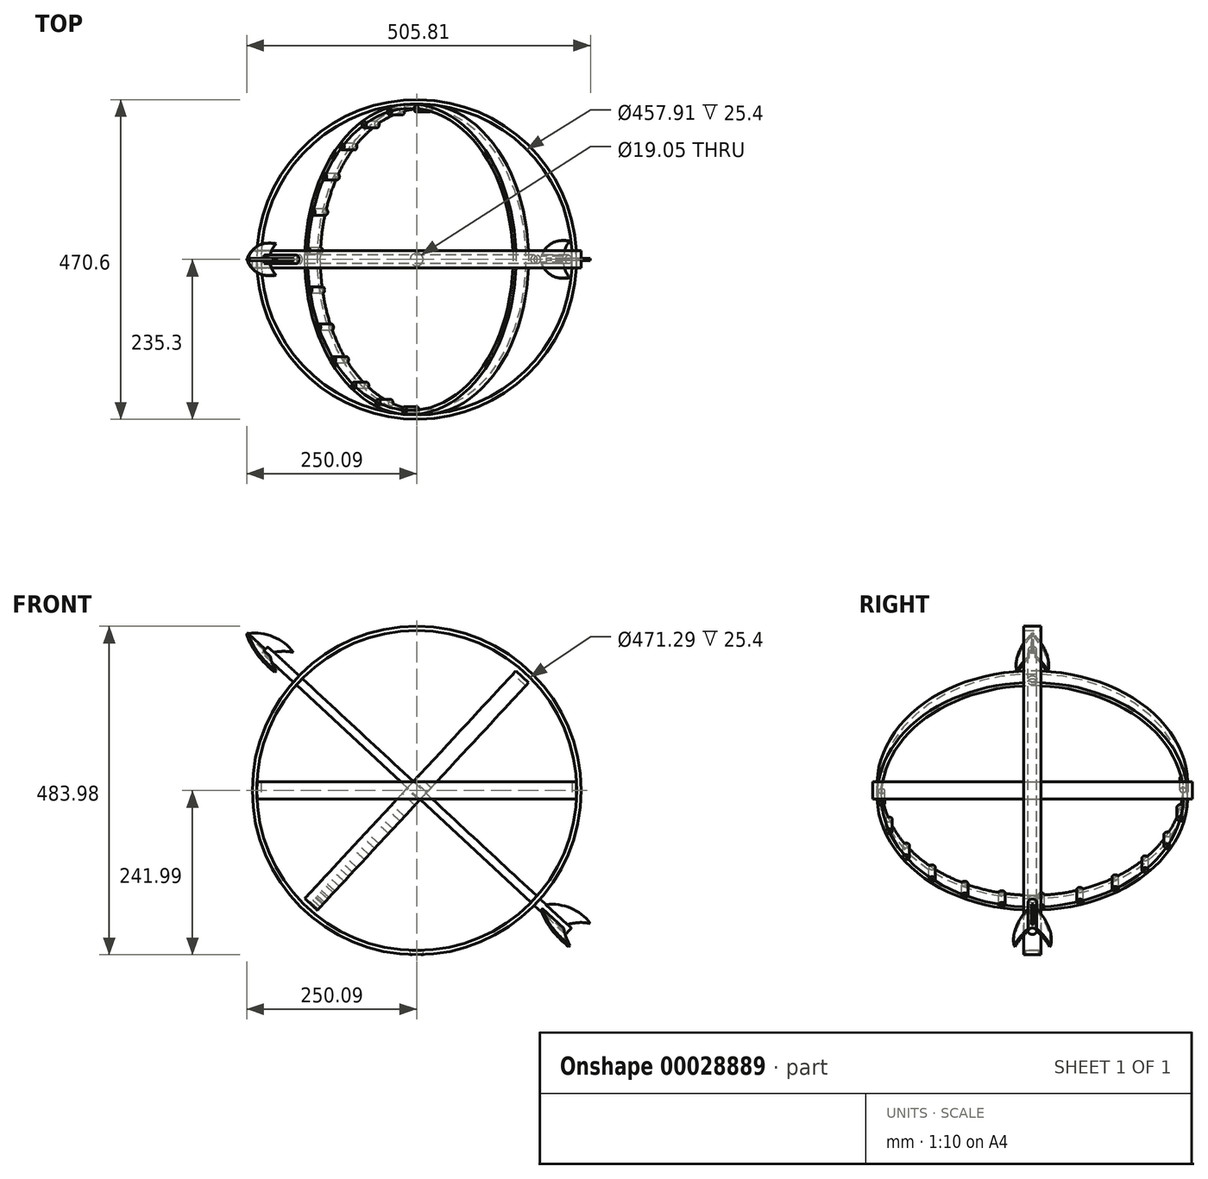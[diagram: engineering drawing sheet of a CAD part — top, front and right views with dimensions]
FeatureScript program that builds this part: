
annotation { "Feature Type Name" : "Feature", "Feature Type Description" : "" }
export const myFeature = defineFeature(function(context is Context, id is Id, definition is map)
    precondition{}
    {
        {
            var Q0;
            Q0=qCreatedBy(makeId("Top.planeOp"),FACE);
            var sketch = newSketch(context, id + "F0", { "sketchPlane" : qUnion([Q0])});
            skLineSegment(sketch, "E0", {"start": v(0, 0) * mm, "end": v(0, -151.73) * mm});
            skSolve(sketch);
        }
        {
            var Q0;
            Q0=sQuery(id+"F0.wireOp",EDGE,"E0");
            cPlane(context, id + "F1", {"entities" : qUnion([Q0]), "cplaneType" : CPlaneType.LINE_ANGLE, "offset" : 152.4 * mm, "angle" : 47.16 * degree, "width" : 152.4 * mm, "height" : 152.4 * mm});
        }
        {
            var Q0;
            Q0=qCreatedBy(id+"F1.planeOp",FACE);
            var sketch = newSketch(context, id + "F2", { "sketchPlane" : qUnion([Q0])});
            skCircle(sketch, "E1", {"center": v(0, 0) * mm, "radius": 222.25 * mm});
            skCircle(sketch, "E2.0", {"center": v(0, 0) * mm, "radius": 228.6 * mm});
            skCircle(sketch, "E3", {"center": v(0, 0) * mm, "radius": 6.35 * mm});
            skSolve(sketch);
        }
        {
            var Q0;
            Q0=makeQuery(id+"F2.imprint","IMPRINT",FACE,{"disambiguationData":[TD([[makeQuery(id+"F2.imprint","IMPRINT",EDGE,{"derivedFrom":sQuery(id+"F2.wireOp",EDGE,"E2.0")}),1.0]])]});
            extrude(context, id + "F3", {"entities" : qUnion([Q0]), "depth" : 12.7 * mm, "hasSecondDirection" : true, "secondDirectionOppositeDirection" : true, "secondDirectionDepth" : 12.7 * mm});
        }
        {
            var Q0;
            Q0=qCreatedBy(makeId("Top.planeOp"),FACE);
            var sketch = newSketch(context, id + "F4", { "sketchPlane" : qUnion([Q0])});
            skCircle(sketch, "E4", {"center": v(0, 0) * mm, "radius": 228.95 * mm});
            skCircle(sketch, "E5.0", {"center": v(0, 0) * mm, "radius": 235.3 * mm});
            skSolve(sketch);
        }
        {
            var Q0;
            Q0=makeQuery(id+"F4.imprint","IMPRINT",FACE,{"disambiguationData":[TD([[makeQuery(id+"F4.imprint","IMPRINT",EDGE,{"derivedFrom":sQuery(id+"F4.wireOp",EDGE,"E4")}),-1.0]])]});
            extrude(context, id + "F5", {"entities" : qUnion([Q0]), "depth" : 12.7 * mm, "hasSecondDirection" : true, "secondDirectionOppositeDirection" : true, "secondDirectionDepth" : 12.7 * mm});
        }
        {
            var Q0;
            Q0=qCreatedBy(makeId("Front.planeOp"),FACE);
            var sketch = newSketch(context, id + "F6", { "sketchPlane" : qUnion([Q0])});
            skCircle(sketch, "E6", {"center": v(0, 0) * mm, "radius": 235.64 * mm});
            skCircle(sketch, "E7.0", {"center": v(0, 0) * mm, "radius": 242 * mm});
            skSolve(sketch);
        }
        {
            var Q0;
            Q0=makeQuery(id+"F6.imprint","IMPRINT",FACE,{"disambiguationData":[TD([[makeQuery(id+"F6.imprint","IMPRINT",EDGE,{"derivedFrom":sQuery(id+"F6.wireOp",EDGE,"E6")}),-1.0]])]});
            extrude(context, id + "F7", {"entities" : qUnion([Q0]), "depth" : 12.7 * mm, "hasSecondDirection" : true, "secondDirectionOppositeDirection" : true, "secondDirectionDepth" : 12.7 * mm});
        }
        {
            var Q0;
            Q0=makeQuery(id+"F2.imprint","IMPRINT",FACE,{"disambiguationData":[TD([[makeQuery(id+"F2.imprint","IMPRINT",EDGE,{"derivedFrom":sQuery(id+"F2.wireOp",EDGE,"E3")}),1.0]])]});
            extrude(context, id + "F8", {"entities" : qUnion([Q0]), "operationType" : NewBodyOperationType.ADD, "depth" : 304.8 * mm, "hasSecondDirection" : true, "secondDirectionOppositeDirection" : true, "secondDirectionDepth" : 304.8 * mm});
        }
        {
            var Q0;
            Q0=qCreatedBy(makeId("Top.planeOp"),FACE);
            cPlane(context, id + "F9", {"entities" : qUnion([Q0]), "cplaneType" : CPlaneType.OFFSET, "offset" : 76.2 * mm, "oppositeDirection" : true, "width" : 152.4 * mm, "height" : 152.4 * mm});
        }
        {
            var Q0;
            Q0=qCreatedBy(id+"F9.planeOp",FACE);
            var sketch = newSketch(context, id + "F10", { "sketchPlane" : qUnion([Q0])});
            skCircle(sketch, "E8", {"center": v(0, 0) * mm, "radius": 9.53 * mm});
            skSolve(sketch);
        }
        {
            var Q0;
            Q0 = qSketchRegion(id + "F10", true);
            extrude(context, id + "F11", {"entities" : qUnion([Q0]), "operationType" : NewBodyOperationType.REMOVE, "oppositeDirection" : true, "depth" : 609.6 * mm});
        }
        {
            var Q0;
            Q0=qCreatedBy(id+"F1.planeOp",FACE);
            var sketch = newSketch(context, id + "F12", { "sketchPlane" : qUnion([Q0])});
            skCircle(sketch, "E9.0", {"center": v(0, 0) * mm, "radius": 222.25 * mm, "construction": true});
            skLineSegment(sketch, "E10", {"start": v(0, 0) * mm, "end": v(0, -222.25) * mm, "construction": true});
            skCircle(sketch, "E11", {"center": v(12.87, -221.88) * mm, "radius": 4.76 * mm});
            skCircle(sketch, "E12.1.0", {"center": v(69.85, -210.99) * mm, "radius": 4.76 * mm});
            skCircle(sketch, "E12.2.0", {"center": v(122.08, -185.72) * mm, "radius": 4.76 * mm});
            skCircle(sketch, "E12.3.0", {"center": v(165.99, -147.8) * mm, "radius": 4.76 * mm});
            skCircle(sketch, "E12.4.0", {"center": v(198.58, -99.8) * mm, "radius": 4.76 * mm});
            skCircle(sketch, "E12.5.0", {"center": v(217.65, -45) * mm, "radius": 4.76 * mm});
            skCircle(sketch, "E12.6.0", {"center": v(221.88, 12.87) * mm, "radius": 4.76 * mm});
            skCircle(sketch, "E12.7.0", {"center": v(210.99, 69.85) * mm, "radius": 4.76 * mm});
            skCircle(sketch, "E12.8.0", {"center": v(185.72, 122.08) * mm, "radius": 4.76 * mm});
            skCircle(sketch, "E12.9.0", {"center": v(147.8, 165.99) * mm, "radius": 4.76 * mm});
            skCircle(sketch, "E12.10.0", {"center": v(99.8, 198.58) * mm, "radius": 4.76 * mm});
            skCircle(sketch, "E12.11.0", {"center": v(45, 217.65) * mm, "radius": 4.76 * mm});
            skCircle(sketch, "E12.12.0", {"center": v(-12.87, 221.88) * mm, "radius": 4.76 * mm});
            skCircle(sketch, "E12.13.0", {"center": v(-69.85, 210.99) * mm, "radius": 4.76 * mm});
            skCircle(sketch, "E12.14.0", {"center": v(-122.08, 185.72) * mm, "radius": 4.76 * mm});
            skCircle(sketch, "E12.15.0", {"center": v(-165.99, 147.8) * mm, "radius": 4.76 * mm});
            skCircle(sketch, "E12.16.0", {"center": v(-198.58, 99.8) * mm, "radius": 4.76 * mm});
            skCircle(sketch, "E12.17.0", {"center": v(-217.65, 45) * mm, "radius": 4.76 * mm});
            skCircle(sketch, "E12.18.0", {"center": v(-221.88, -12.87) * mm, "radius": 4.76 * mm});
            skCircle(sketch, "E12.19.0", {"center": v(-210.99, -69.85) * mm, "radius": 4.76 * mm});
            skCircle(sketch, "E12.20.0", {"center": v(-185.72, -122.08) * mm, "radius": 4.76 * mm});
            skCircle(sketch, "E12.21.0", {"center": v(-147.8, -165.99) * mm, "radius": 4.76 * mm});
            skCircle(sketch, "E12.22.0", {"center": v(-99.8, -198.58) * mm, "radius": 4.76 * mm});
            skCircle(sketch, "E12.23.0", {"center": v(-45, -217.65) * mm, "radius": 4.76 * mm});
            skLineSegment(sketch, "E13", {"start": v(0, 0) * mm, "end": v(12.87, -221.88) * mm, "construction": true});
            skSolve(sketch);
        }
        {
            var Q0;
            Q0=makeQuery(id+"F12.imprint","IMPRINT",FACE,{"disambiguationData":[TD([[makeQuery(id+"F12.imprint","IMPRINT",EDGE,{"derivedFrom":sQuery(id+"F12.wireOp",EDGE,"E11")}),1.0]])]});
            var Q1;
            Q1=makeQuery(id+"F12.imprint","IMPRINT",FACE,{"disambiguationData":[TD([[makeQuery(id+"F12.imprint","IMPRINT",EDGE,{"derivedFrom":sQuery(id+"F12.wireOp",EDGE,"E12.1.0")}),1.0]])]});
            var Q2;
            Q2=makeQuery(id+"F12.imprint","IMPRINT",FACE,{"disambiguationData":[TD([[makeQuery(id+"F12.imprint","IMPRINT",EDGE,{"derivedFrom":sQuery(id+"F12.wireOp",EDGE,"E12.2.0")}),1.0]])]});
            var Q3;
            Q3=makeQuery(id+"F12.imprint","IMPRINT",FACE,{"disambiguationData":[TD([[makeQuery(id+"F12.imprint","IMPRINT",EDGE,{"derivedFrom":sQuery(id+"F12.wireOp",EDGE,"E12.3.0")}),1.0]])]});
            var Q4;
            Q4=makeQuery(id+"F12.imprint","IMPRINT",FACE,{"disambiguationData":[TD([[makeQuery(id+"F12.imprint","IMPRINT",EDGE,{"derivedFrom":sQuery(id+"F12.wireOp",EDGE,"E12.23.0")}),1.0]])]});
            var Q5;
            Q5=makeQuery(id+"F12.imprint","IMPRINT",FACE,{"disambiguationData":[TD([[makeQuery(id+"F12.imprint","IMPRINT",EDGE,{"derivedFrom":sQuery(id+"F12.wireOp",EDGE,"E12.4.0")}),1.0]])]});
            var Q6;
            Q6=makeQuery(id+"F12.imprint","IMPRINT",FACE,{"disambiguationData":[TD([[makeQuery(id+"F12.imprint","IMPRINT",EDGE,{"derivedFrom":sQuery(id+"F12.wireOp",EDGE,"E12.5.0")}),1.0]])]});
            var Q7;
            Q7=makeQuery(id+"F12.imprint","IMPRINT",FACE,{"disambiguationData":[TD([[makeQuery(id+"F12.imprint","IMPRINT",EDGE,{"derivedFrom":sQuery(id+"F12.wireOp",EDGE,"E12.22.0")}),1.0]])]});
            var Q8;
            Q8=makeQuery(id+"F12.imprint","IMPRINT",FACE,{"disambiguationData":[TD([[makeQuery(id+"F12.imprint","IMPRINT",EDGE,{"derivedFrom":sQuery(id+"F12.wireOp",EDGE,"E12.21.0")}),1.0]])]});
            var Q9;
            Q9=makeQuery(id+"F12.imprint","IMPRINT",FACE,{"disambiguationData":[TD([[makeQuery(id+"F12.imprint","IMPRINT",EDGE,{"derivedFrom":sQuery(id+"F12.wireOp",EDGE,"E12.20.0")}),1.0]])]});
            var Q10;
            Q10=makeQuery(id+"F12.imprint","IMPRINT",FACE,{"disambiguationData":[TD([[makeQuery(id+"F12.imprint","IMPRINT",EDGE,{"derivedFrom":sQuery(id+"F12.wireOp",EDGE,"E12.19.0")}),1.0]])]});
            var Q11;
            Q11=makeQuery(id+"F12.imprint","IMPRINT",FACE,{"disambiguationData":[TD([[makeQuery(id+"F12.imprint","IMPRINT",EDGE,{"derivedFrom":sQuery(id+"F12.wireOp",EDGE,"E12.6.0")}),1.0]])]});
            var Q12;
            Q12=makeQuery(id+"F12.imprint","IMPRINT",FACE,{"disambiguationData":[TD([[makeQuery(id+"F12.imprint","IMPRINT",EDGE,{"derivedFrom":sQuery(id+"F12.wireOp",EDGE,"E12.18.0")}),1.0]])]});
            extrude(context, id + "F13", {"entities" : qUnion([Q0, Q1, Q2, Q3, Q4, Q5, Q6, Q7, Q8, Q9, Q10, Q11, Q12]), "depth" : 12.7 * mm, "hasSecondDirection" : true, "secondDirectionOppositeDirection" : true, "secondDirectionDepth" : 12.7 * mm});
        }
        {
            var Q0;
            Q0=qCreatedBy(makeId("Front.planeOp"),FACE);
            var sketch = newSketch(context, id + "F14", { "sketchPlane" : qUnion([Q0])});
            skLineSegment(sketch, "E14", {"start": v(181.7, -159.83) * mm, "end": v(227.81, -202.6) * mm, "construction": true});
            skLineSegment(sketch, "E15", {"start": v(219.18, -211.9) * mm, "end": v(173.07, -169.14) * mm, "construction": true});
            skLineSegment(sketch, "E16.0", {"start": v(227.81, -202.6) * mm, "end": v(219.18, -211.9) * mm, "construction": true});
            skCircle(sketch, "E17", {"center": v(198.96, -238.59) * mm, "radius": 71.03 * mm});
            skCircle(sketch, "E18", {"center": v(241.88, -260.98) * mm, "radius": 66.56 * mm});
            skLineSegment(sketch, "E19", {"start": v(226.68, -203.82) * mm, "end": v(180.61, -161.1) * mm});
            skSolve(sketch);
        }
        {
            var Q0;
            {var subQ0=sQuery(id+"F14.wireOp",EDGE,"E19");var subQ3=sQuery(id+"F14.wireOp",EDGE,"E17");var subQ4=makeQuery(id+"F14.imprint","INTERSECT",VERTEX,{"derivedFrom":[subQ3,subQ0]});Q0=makeQuery(id+"F14.imprint","IMPRINT",FACE,{"disambiguationData":[TD([[makeQuery(id+"F14.imprint","IMPRINT",EDGE,{"disambiguationData":[TD([[subQ4,1.0]])],"derivedFrom":subQ3}),1.0]])]});}
            extrude(context, id + "F15", {"entities" : qUnion([Q0]), "depth" : 1.59 * mm, "hasSecondDirection" : true, "secondDirectionOppositeDirection" : true, "secondDirectionDepth" : 1.59 * mm});
        }
        {
            var Q0;
            Q0=makeQuery(id+"F15.opExtrude","SWEPT_BODY",BODY,{"disambiguationData":[OSD([sQuery(id+"F14.wireOp",EDGE,"E14"),sQuery(id+"F14.wireOp",EDGE,"E17"),sQuery(id+"F14.wireOp",EDGE,"E18")])]});
            var Q1;
            Q1=makeQuery(id+"F8.opExtrude","CAP_EDGE",EDGE,{"disambiguationData":[OSD([sQuery(id+"F2.wireOp",EDGE,"E3")])],"isStart":false});
            var Q2;
            Q2=makeQuery(id+"F7.opExtrude","SWEPT_BODY",BODY,{"disambiguationData":[OSD([sQuery(id+"F6.wireOp",EDGE,"E6"),sQuery(id+"F6.wireOp",EDGE,"E7.0")])]});
            circularPattern(context, id + "F16", {"operationType" : NewBodyOperationType.ADD, "entities" : qUnion([Q0]), "axis" : qUnion([Q1]), "angle" : 120 * degree, "instanceCount" : 3});
        }
        {
            var Q0;
            Q0=qCreatedBy(makeId("Front.planeOp"),FACE);
            var sketch = newSketch(context, id + "F17", { "sketchPlane" : qUnion([Q0])});
            skLineSegment(sketch, "E20", {"start": v(-255.58, 239.59) * mm, "end": v(-209.47, 196.83) * mm, "construction": true});
            skLineSegment(sketch, "E21", {"start": v(-218.1, 187.52) * mm, "end": v(-264.21, 230.28) * mm, "construction": true});
            skLineSegment(sketch, "E22.0", {"start": v(-209.62, 196.66) * mm, "end": v(-218.25, 187.35) * mm, "construction": true});
            skCircle(sketch, "E23", {"center": v(-238.32, 160.84) * mm, "radius": 71.03 * mm});
            skCircle(sketch, "E24", {"center": v(-195.4, 138.44) * mm, "radius": 66.56 * mm});
            skLineSegment(sketch, "E25", {"start": v(-210.76, 195.44) * mm, "end": v(-302.12, 280.16) * mm});
            skLineSegment(sketch, "E26.0", {"start": v(-219.18, 211.9) * mm, "end": v(-227.81, 202.6) * mm});
            skPoint(sketch, "E27", {"position": v(-223.5, 207.25) * mm});
            skSolve(sketch);
        }
        {
            var Q0;
            {var subQ0=sQuery(id+"F17.wireOp",EDGE,"E25");var subQ1=makeQuery(id+"F17.imprint","IMPRINT",VERTEX,{"derivedFrom":subQ0});Q0=makeQuery(id+"F17.imprint","IMPRINT",FACE,{"disambiguationData":[TD([[makeQuery(id+"F17.imprint","IMPRINT",EDGE,{"disambiguationData":[TD([[subQ1,1.0]])],"derivedFrom":subQ0}),-1.0]])]});}
            extrude(context, id + "F18", {"entities" : qUnion([Q0]), "depth" : 1.59 * mm, "hasSecondDirection" : true, "secondDirectionOppositeDirection" : true, "secondDirectionDepth" : 1.59 * mm});
        }
        {
            var Q0;
            Q0=makeQuery(id+"F18.opExtrude","SWEPT_BODY",BODY,{"disambiguationData":[OSD([sQuery(id+"F17.wireOp",EDGE,"E23"),sQuery(id+"F17.wireOp",EDGE,"E24"),sQuery(id+"F17.wireOp",EDGE,"E25")])]});
            var Q1;
            Q1=sQuery(id+"F17.wireOp",EDGE,"E25");
            circularPattern(context, id + "F19", {"operationType" : NewBodyOperationType.ADD, "entities" : qUnion([Q0]), "axis" : qUnion([Q1]), "angle" : 120 * degree, "instanceCount" : 3});
        }
    });
